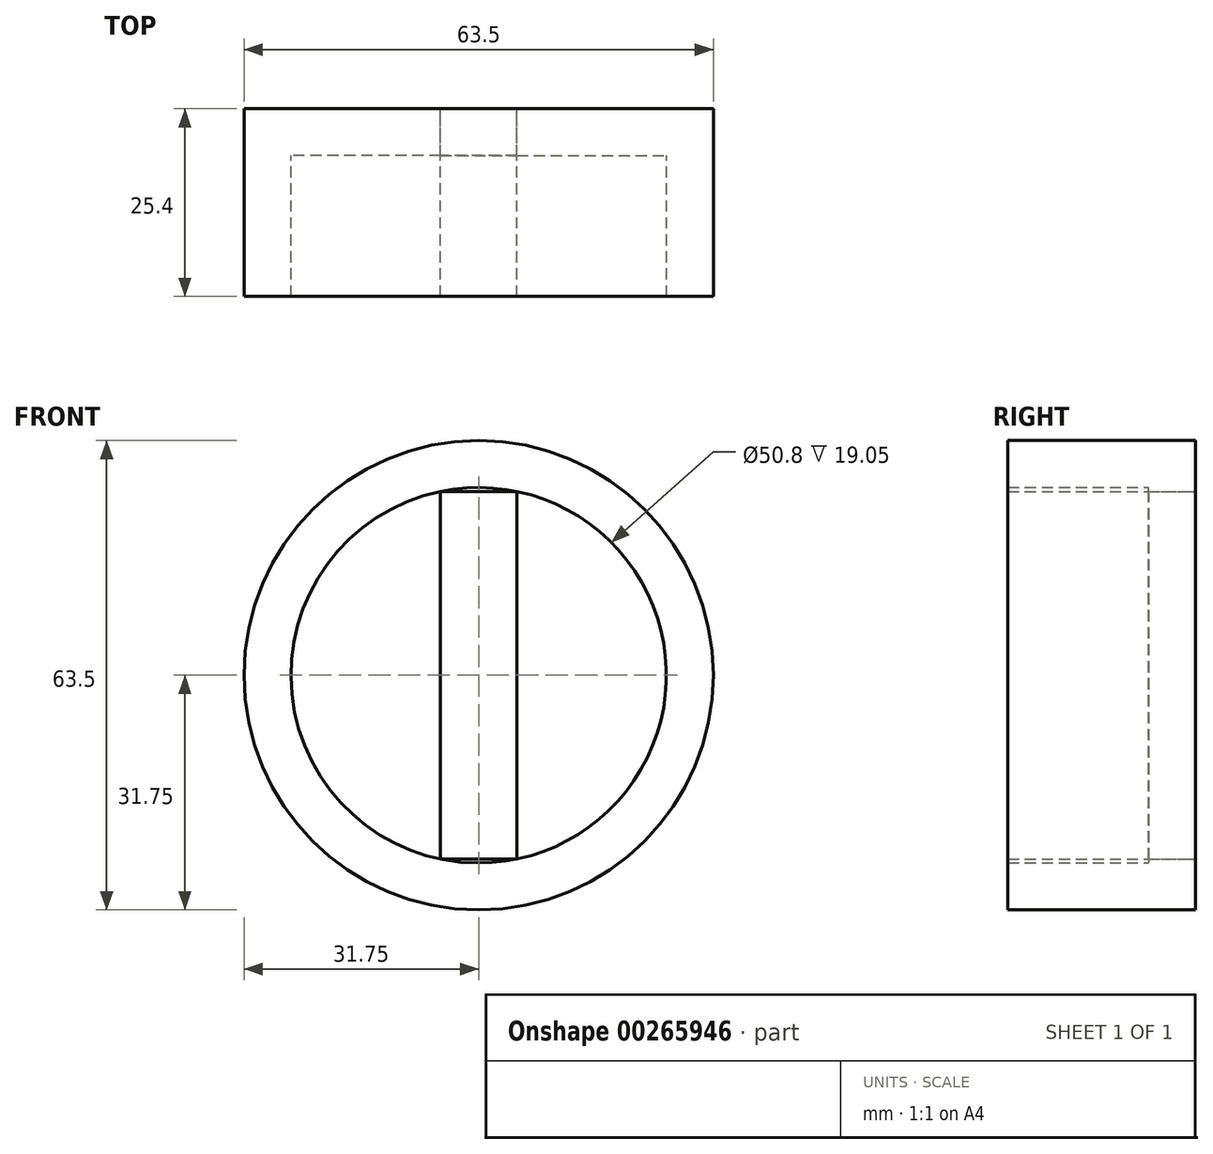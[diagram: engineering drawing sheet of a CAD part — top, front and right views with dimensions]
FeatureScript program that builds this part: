
annotation { "Feature Type Name" : "Feature", "Feature Type Description" : "" }
export const myFeature = defineFeature(function(context is Context, id is Id, definition is map)
    precondition{}
    {
        {
            var Q0;
            Q0=qCreatedBy(makeId("Front.planeOp"),FACE);
            var sketch = newSketch(context, id + "F0", { "sketchPlane" : qUnion([Q0])});
            skCircle(sketch, "E0", {"center": v(0, 0) * mm, "radius": 31.75 * mm});
            skCircle(sketch, "E1", {"center": v(0, 0) * mm, "radius": 25.4 * mm});
            skLineSegment(sketch, "E2.bottom", {"start": v(-5.17, 24.87) * mm, "end": v(5.17, 24.87) * mm});
            skLineSegment(sketch, "E2.top", {"start": v(-5.17, -24.87) * mm, "end": v(5.17, -24.87) * mm});
            skLineSegment(sketch, "E2.left", {"start": v(-5.17, 24.87) * mm, "end": v(-5.17, -24.87) * mm});
            skLineSegment(sketch, "E2.right", {"start": v(5.17, 24.87) * mm, "end": v(5.17, -24.87) * mm});
            skSolve(sketch);
        }
        {
            var Q0;
            Q0=makeQuery(id+"F0.imprint","IMPRINT",FACE,{"disambiguationData":[TD([[makeQuery(id+"F0.imprint","IMPRINT",EDGE,{"derivedFrom":sQuery(id+"F0.wireOp",EDGE,"E0")}),1.0]])]});
            extrude(context, id + "F1", {"entities" : qUnion([Q0]), "depth" : 25.4 * mm});
        }
        {
            var Q0;
            Q0=makeQuery(id+"F0.imprint","IMPRINT",FACE,{"disambiguationData":[TD([[makeQuery(id+"F0.imprint","IMPRINT",EDGE,{"derivedFrom":sQuery(id+"F0.wireOp",EDGE,"E1")}),1.0]])]});
            extrude(context, id + "F2", {"entities" : qUnion([Q0]), "operationType" : NewBodyOperationType.ADD, "depth" : 6.35 * mm});
        }
        {
            var Q0;
            Q0=makeQuery(id+"F0.imprint","IMPRINT",FACE,{"disambiguationData":[TD([[makeQuery(id+"F0.imprint","IMPRINT",EDGE,{"derivedFrom":sQuery(id+"F0.wireOp",EDGE,"E2.bottom")}),-1.0]])]});
            extrude(context, id + "F3", {"entities" : qUnion([Q0]), "depth" : 25.4 * mm});
        }
    });
